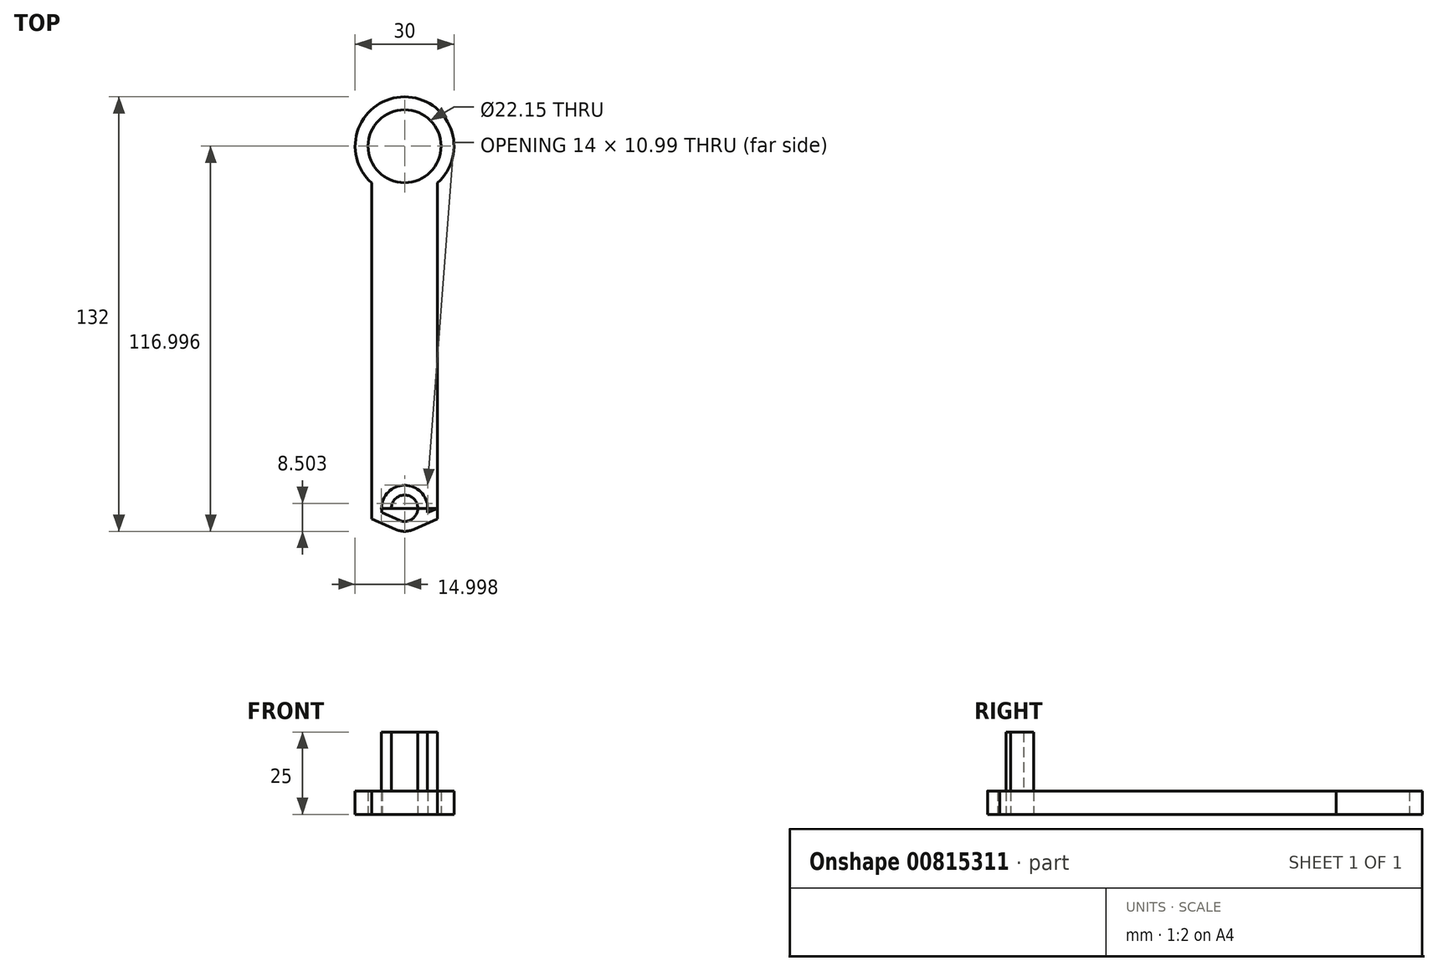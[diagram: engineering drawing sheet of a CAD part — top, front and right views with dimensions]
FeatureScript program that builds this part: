
annotation { "Feature Type Name" : "Feature", "Feature Type Description" : "" }
export const myFeature = defineFeature(function(context is Context, id is Id, definition is map)
    precondition{}
    {
        {
            var Q0;
            Q0=qCreatedBy(makeId("Top.planeOp"),FACE);
            var sketch = newSketch(context, id + "F0", { "sketchPlane" : qUnion([Q0])});
            skLineSegment(sketch, "E0.bottom", {"start": v(-8.75, -69.11) * mm, "end": v(11.25, -69.11) * mm});
            skLineSegment(sketch, "E0.top", {"start": v(-8.75, 40.89) * mm, "end": v(11.25, 40.89) * mm});
            skLineSegment(sketch, "E0.left", {"start": v(-8.75, -69.11) * mm, "end": v(-8.75, 40.89) * mm});
            skLineSegment(sketch, "E0.right", {"start": v(11.25, -69.11) * mm, "end": v(11.25, 40.89) * mm});
            skCircle(sketch, "E1", {"center": v(1.25, 40.89) * mm, "radius": 15 * mm});
            skCircle(sketch, "E2", {"center": v(1.25, 40.89) * mm, "radius": 11.07 * mm});
            skLineSegment(sketch, "E3", {"start": v(-8.75, -69.11) * mm, "end": v(1.25, -69.11) * mm});
            skCircle(sketch, "E4", {"center": v(1.25, -69.11) * mm, "radius": 4 * mm});
            skLineSegment(sketch, "E5", {"start": v(-8.75, -69.11) * mm, "end": v(-0.35, -72.78) * mm});
            skLineSegment(sketch, "E6", {"start": v(11.25, -69.11) * mm, "end": v(2.85, -72.78) * mm});
            skLineSegment(sketch, "E7", {"start": v(-8.75, -69.11) * mm, "end": v(-8.75, -72.53) * mm});
            skLineSegment(sketch, "E8", {"start": v(11.25, -69.11) * mm, "end": v(11.25, -72.8) * mm});
            skCircle(sketch, "E9.0", {"center": v(1.25, -69.11) * mm, "radius": 7 * mm});
            skLineSegment(sketch, "E10.0", {"start": v(-9.95, -71.86) * mm, "end": v(-1.55, -75.53) * mm});
            skLineSegment(sketch, "E11.0", {"start": v(12.45, -71.86) * mm, "end": v(4.05, -75.53) * mm});
            skSolve(sketch);
        }
        {
            var Q0;
            {var subQ0=sQuery(id+"F0.wireOp",EDGE,"E1");var subQ1=sQuery(id+"F0.wireOp",EDGE,"E0.left");var subQ2=makeQuery(id+"F0.imprint","INTERSECT",VERTEX,{"derivedFrom":[subQ1,subQ0]});Q0=makeQuery(id+"F0.imprint","IMPRINT",FACE,{"disambiguationData":[TD([[makeQuery(id+"F0.imprint","IMPRINT",EDGE,{"disambiguationData":[TD([[subQ2,-1.0]])],"derivedFrom":subQ1}),1.0]])]});}
            var Q1;
            {var subQ0=sQuery(id+"F0.wireOp",EDGE,"E1");var subQ1=sQuery(id+"F0.wireOp",EDGE,"E0.left");var subQ2=makeQuery(id+"F0.imprint","INTERSECT",VERTEX,{"derivedFrom":[subQ1,subQ0]});Q1=makeQuery(id+"F0.imprint","IMPRINT",FACE,{"disambiguationData":[TD([[makeQuery(id+"F0.imprint","IMPRINT",EDGE,{"disambiguationData":[TD([[subQ2,-1.0]])],"derivedFrom":subQ1}),-1.0]])]});}
            var Q2;
            {var subQ0=sQuery(id+"F0.wireOp",EDGE,"E1");var subQ1=sQuery(id+"F0.wireOp",EDGE,"E0.left");var subQ2=makeQuery(id+"F0.imprint","INTERSECT",VERTEX,{"derivedFrom":[subQ1,subQ0]});Q2=makeQuery(id+"F0.imprint","IMPRINT",FACE,{"disambiguationData":[TD([[makeQuery(id+"F0.imprint","IMPRINT",EDGE,{"disambiguationData":[TD([[subQ2,-1.0]])],"derivedFrom":subQ0}),-1.0]])]});}
            var Q3;
            {var subQ0=sQuery(id+"F0.wireOp",EDGE,"E4");var subQ1=sQuery(id+"F0.wireOp",EDGE,"E0.bottom");var subQ2=makeQuery(id+"F0.imprint","INTERSECT",VERTEX,{"derivedFrom":[subQ1,subQ0]});Q3=makeQuery(id+"F0.imprint","IMPRINT",FACE,{"disambiguationData":[TD([[makeQuery(id+"F0.imprint","IMPRINT",EDGE,{"disambiguationData":[TD([[subQ2,-1.0]])],"derivedFrom":subQ1}),1.0]])]});}
            var Q4;
            {var subQ0=sQuery(id+"F0.wireOp",EDGE,"E5");var subQ1=sQuery(id+"F0.wireOp",EDGE,"E4");var subQ2=makeQuery(id+"F0.imprint","INTERSECT",VERTEX,{"derivedFrom":[subQ1,subQ0]});Q4=makeQuery(id+"F0.imprint","IMPRINT",FACE,{"disambiguationData":[TD([[makeQuery(id+"F0.imprint","IMPRINT",EDGE,{"disambiguationData":[TD([[subQ2,-1.0]])],"derivedFrom":subQ1}),-1.0]])]});}
            var Q5;
            {var subQ3=sQuery(id+"F0.wireOp",EDGE,"E9.0");var subQ5=sQuery(id+"F0.wireOp",EDGE,"E11.0");var subQ7=makeQuery(id+"F0.imprint","INTERSECT",VERTEX,{"derivedFrom":[subQ3,subQ5]});Q5=makeQuery(id+"F0.imprint","IMPRINT",FACE,{"disambiguationData":[TD([[makeQuery(id+"F0.imprint","IMPRINT",EDGE,{"disambiguationData":[TD([[subQ7,-1.0]])],"derivedFrom":subQ3}),-1.0]])]});}
            var Q6;
            {var subQ0=sQuery(id+"F0.wireOp",EDGE,"E9.0");var subQ1=sQuery(id+"F0.wireOp",EDGE,"E3");var subQ2=makeQuery(id+"F0.imprint","INTERSECT",VERTEX,{"derivedFrom":[subQ1,subQ0]});Q6=makeQuery(id+"F0.imprint","IMPRINT",FACE,{"disambiguationData":[TD([[makeQuery(id+"F0.imprint","IMPRINT",EDGE,{"disambiguationData":[TD([[subQ2,-1.0]])],"derivedFrom":subQ1}),-1.0]])]});}
            var Q7;
            {var subQ0=sQuery(id+"F0.wireOp",EDGE,"E4");var subQ1=sQuery(id+"F0.wireOp",EDGE,"E0.bottom");var subQ2=makeQuery(id+"F0.imprint","INTERSECT",VERTEX,{"derivedFrom":[subQ1,subQ0]});Q7=makeQuery(id+"F0.imprint","IMPRINT",FACE,{"disambiguationData":[TD([[makeQuery(id+"F0.imprint","IMPRINT",EDGE,{"disambiguationData":[TD([[subQ2,-1.0]])],"derivedFrom":subQ1}),-1.0]])]});}
            var Q8;
            {var subQ3=sQuery(id+"F0.wireOp",EDGE,"E9.0");var subQ5=sQuery(id+"F0.wireOp",EDGE,"E10.0");var subQ7=makeQuery(id+"F0.imprint","INTERSECT",VERTEX,{"derivedFrom":[subQ3,subQ5]});Q8=makeQuery(id+"F0.imprint","IMPRINT",FACE,{"disambiguationData":[TD([[makeQuery(id+"F0.imprint","IMPRINT",EDGE,{"disambiguationData":[TD([[subQ7,1.0]])],"derivedFrom":subQ3}),-1.0]])]});}
            var Q9;
            {var subQ1=sQuery(id+"F0.wireOp",EDGE,"E3");var subQ3=sQuery(id+"F0.wireOp",EDGE,"E9.0");var subQ4=makeQuery(id+"F0.imprint","INTERSECT",VERTEX,{"derivedFrom":[subQ1,subQ3]});Q9=makeQuery(id+"F0.imprint","IMPRINT",FACE,{"disambiguationData":[TD([[makeQuery(id+"F0.imprint","IMPRINT",EDGE,{"disambiguationData":[TD([[subQ4,-1.0]])],"derivedFrom":subQ3}),-1.0]])]});}
            var Q10;
            {var subQ1=sQuery(id+"F0.wireOp",EDGE,"E0.bottom");var subQ3=sQuery(id+"F0.wireOp",EDGE,"E9.0");var subQ4=makeQuery(id+"F0.imprint","INTERSECT",VERTEX,{"derivedFrom":[subQ1,subQ3]});Q10=makeQuery(id+"F0.imprint","IMPRINT",FACE,{"disambiguationData":[TD([[makeQuery(id+"F0.imprint","IMPRINT",EDGE,{"disambiguationData":[TD([[subQ4,1.0]])],"derivedFrom":subQ3}),-1.0]])]});}
            extrude(context, id + "F1", {"entities" : qUnion([Q0, Q1, Q2, Q3, Q4, Q5, Q6, Q7, Q8, Q9, Q10]), "depth" : 7.1 * mm, "offsetDistance" : 25 * mm});
        }
        {
            var Q0;
            {var subQ0=sQuery(id+"F0.wireOp",EDGE,"E3");var subQ1=sQuery(id+"F0.wireOp",EDGE,"E0.bottom");var subQ2=makeQuery(id+"F0.imprint","INTERSECT",VERTEX,{"derivedFrom":[subQ1,subQ0]});Q0=makeQuery(id+"F0.imprint","IMPRINT",FACE,{"disambiguationData":[TD([[makeQuery(id+"F0.imprint","IMPRINT",EDGE,{"disambiguationData":[TD([[subQ2,-1.0]])],"derivedFrom":subQ1}),1.0]])]});}
            var Q1;
            {var subQ3=sQuery(id+"F0.wireOp",EDGE,"E3");var subQ5=sQuery(id+"F0.wireOp",EDGE,"E0.bottom");var subQ6=makeQuery(id+"F0.imprint","INTERSECT",VERTEX,{"derivedFrom":[subQ5,subQ3]});Q1=makeQuery(id+"F0.imprint","IMPRINT",FACE,{"disambiguationData":[TD([[makeQuery(id+"F0.imprint","IMPRINT",EDGE,{"disambiguationData":[TD([[subQ6,-1.0]])],"derivedFrom":subQ5}),-1.0]])]});}
            extrude(context, id + "F2", {"entities" : qUnion([Q0, Q1]), "operationType" : NewBodyOperationType.ADD, "depth" : 25 * mm, "offsetDistance" : 25 * mm});
        }
    });
